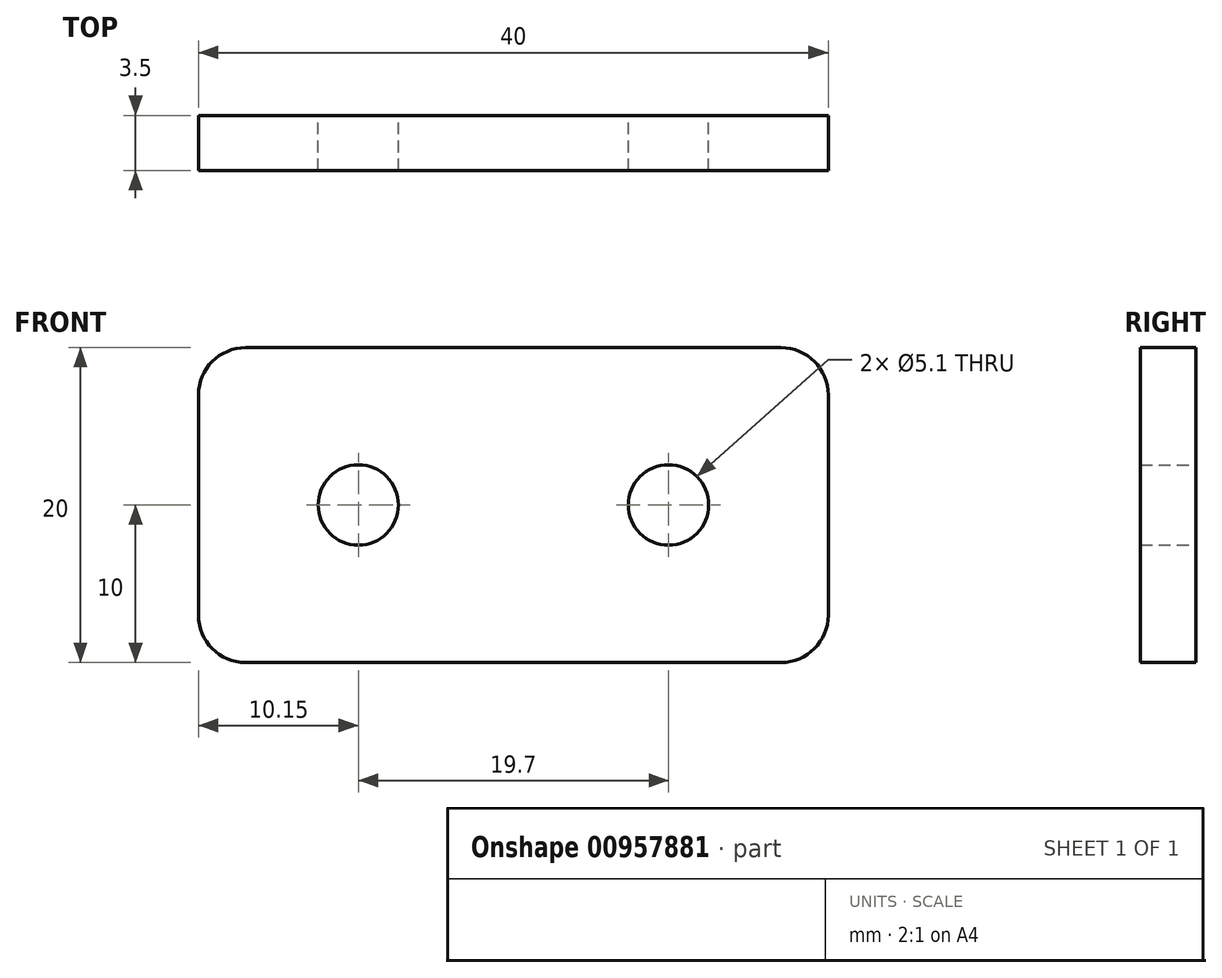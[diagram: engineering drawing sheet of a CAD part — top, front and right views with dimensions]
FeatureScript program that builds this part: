
annotation { "Feature Type Name" : "Feature", "Feature Type Description" : "" }
export const myFeature = defineFeature(function(context is Context, id is Id, definition is map)
    precondition{}
    {
        {
            var Q0;
            Q0=qCreatedBy(makeId("Front.planeOp"),FACE);
            var sketch = newSketch(context, id + "F0", { "sketchPlane" : qUnion([Q0])});
            skLineSegment(sketch, "E0.bottom", {"start": v(-20, 10) * mm, "end": v(20, 10) * mm});
            skLineSegment(sketch, "E0.top", {"start": v(-20, -10) * mm, "end": v(20, -10) * mm});
            skLineSegment(sketch, "E0.left", {"start": v(-20, 10) * mm, "end": v(-20, -10) * mm});
            skLineSegment(sketch, "E0.right", {"start": v(20, 10) * mm, "end": v(20, -10) * mm});
            skPoint(sketch, "E0.middle", {"position": v(0, 0) * mm});
            skCircle(sketch, "E1", {"center": v(-9.85, 0) * mm, "radius": 2.55 * mm});
            skCircle(sketch, "E2", {"center": v(9.85, 0) * mm, "radius": 2.55 * mm});
            skSolve(sketch);
        }
        {
            var Q0;
            Q0=makeQuery(id+"F0.imprint","IMPRINT",FACE,{"disambiguationData":[TD([[makeQuery(id+"F0.imprint","IMPRINT",EDGE,{"derivedFrom":sQuery(id+"F0.wireOp",EDGE,"E0.bottom")}),-1.0]])]});
            extrude(context, id + "F1", {"entities" : qUnion([Q0]), "depth" : 3.5 * mm, "offsetDistance" : 25 * mm});
        }
        {
            var Q0;
            Q0=makeQuery(id+"F1.opExtrude","SWEPT_EDGE",EDGE,{"disambiguationData":[OSD([sQuery(id+"F0.wireOp",EDGE,"E0.bottom"),sQuery(id+"F0.wireOp",EDGE,"E0.left")])]});
            var Q1;
            Q1=makeQuery(id+"F1.opExtrude","SWEPT_EDGE",EDGE,{"disambiguationData":[OSD([sQuery(id+"F0.wireOp",EDGE,"E0.top"),sQuery(id+"F0.wireOp",EDGE,"E0.left")])]});
            var Q2;
            Q2=makeQuery(id+"F1.opExtrude","SWEPT_EDGE",EDGE,{"disambiguationData":[OSD([sQuery(id+"F0.wireOp",EDGE,"E0.top"),sQuery(id+"F0.wireOp",EDGE,"E0.right")])]});
            var Q3;
            Q3=makeQuery(id+"F1.opExtrude","SWEPT_EDGE",EDGE,{"disambiguationData":[OSD([sQuery(id+"F0.wireOp",EDGE,"E0.bottom"),sQuery(id+"F0.wireOp",EDGE,"E0.right")])]});
            fillet(context, id + "F2", {"entities" : qUnion([Q0, Q1, Q2, Q3]), "radius" : 3 * mm, "tangentPropagation" : true, "allowEdgeOverflow" : false});
        }
    });
